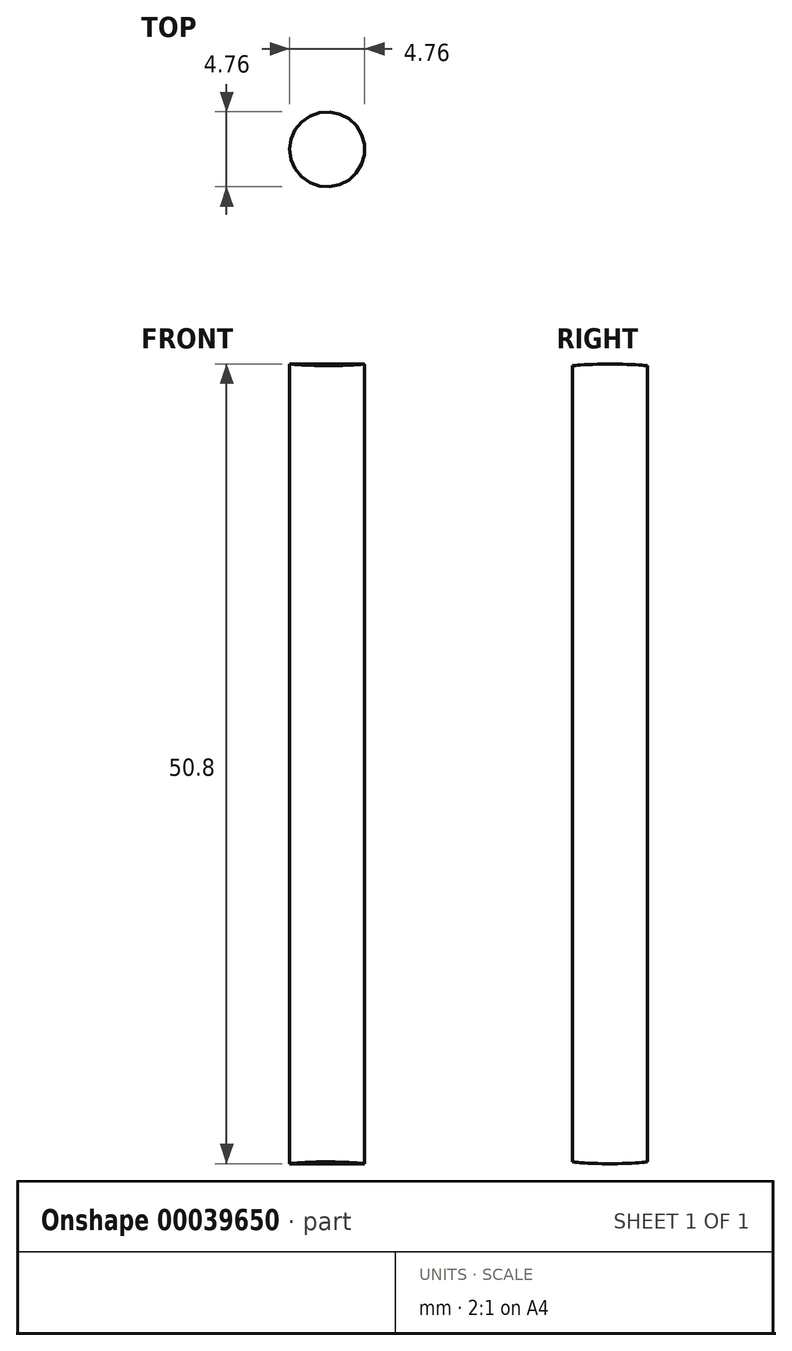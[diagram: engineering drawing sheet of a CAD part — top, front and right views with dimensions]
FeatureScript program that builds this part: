
annotation { "Feature Type Name" : "Feature", "Feature Type Description" : "" }
export const myFeature = defineFeature(function(context is Context, id is Id, definition is map)
    precondition{}
    {
        {
            var Q0;
            Q0=qCreatedBy(makeId("Top.planeOp"),FACE);
            var sketch = newSketch(context, id + "F0", { "sketchPlane" : qUnion([Q0])});
            skCircle(sketch, "E0", {"center": v(0, 0) * mm, "radius": 2.38 * mm});
            skSolve(sketch);
        }
        {
            var Q0;
            Q0 = qSketchRegion(id + "F0", true);
            extrude(context, id + "F1", {"entities" : qUnion([Q0]), "depth" : 50.8 * mm});
        }
        {
            var Q0;
            Q0=qCreatedBy(makeId("Right.planeOp"),FACE);
            var sketch = newSketch(context, id + "F2", { "sketchPlane" : qUnion([Q0])});
            skLineSegment(sketch, "E1", {"start": v(0, 0) * mm, "end": v(0, 25.4) * mm});
            skCircle(sketch, "E2", {"center": v(0, 25.4) * mm, "radius": 25.4 * mm});
            skCircle(sketch, "E3", {"center": v(0, 25.4) * mm, "radius": 31.92 * mm});
            skSolve(sketch);
        }
        {
            var Q0;
            Q0=makeQuery(id+"F2.imprint","IMPRINT",FACE,{"disambiguationData":[TD([[makeQuery(id+"F2.imprint","IMPRINT",EDGE,{"derivedFrom":sQuery(id+"F2.wireOp",EDGE,"E2")}),-1.0]])]});
            extrude(context, id + "F3", {"entities" : qUnion([Q0]), "operationType" : NewBodyOperationType.REMOVE, "endBound" : BoundingType.SYMMETRIC, "oppositeDirection" : true, "depth" : 25.4 * mm});
        }
    });
